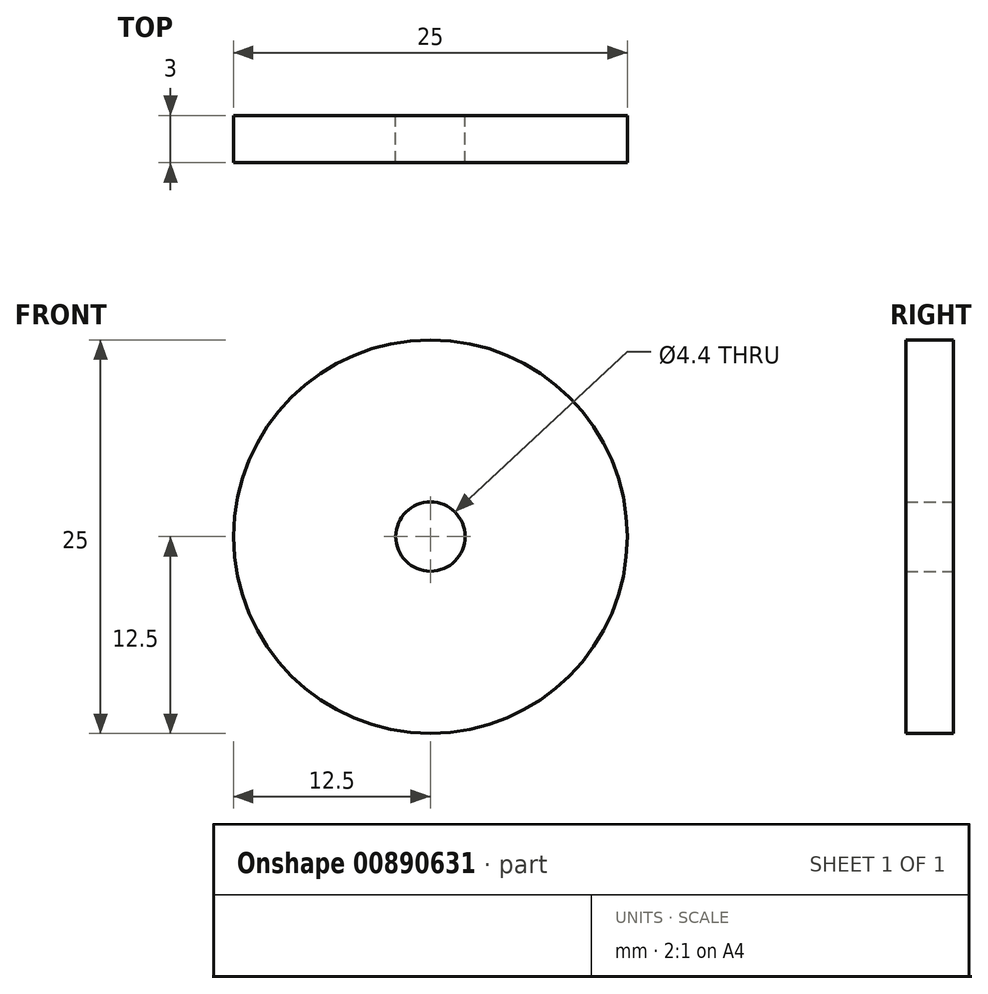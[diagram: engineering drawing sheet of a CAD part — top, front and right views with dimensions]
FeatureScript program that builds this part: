
annotation { "Feature Type Name" : "Feature", "Feature Type Description" : "" }
export const myFeature = defineFeature(function(context is Context, id is Id, definition is map)
    precondition{}
    {
        {
            var Q0;
            Q0=qCreatedBy(makeId("Front.planeOp"),FACE);
            var sketch = newSketch(context, id + "F0", { "sketchPlane" : qUnion([Q0])});
            skCircle(sketch, "E0", {"center": v(0, 0) * mm, "radius": 12.5 * mm});
            skCircle(sketch, "E1", {"center": v(0, 0) * mm, "radius": 2.2 * mm});
            skSolve(sketch);
        }
        {
            var Q0;
            Q0=makeQuery(id+"F0.imprint","IMPRINT",FACE,{"disambiguationData":[TD([[makeQuery(id+"F0.imprint","IMPRINT",EDGE,{"derivedFrom":sQuery(id+"F0.wireOp",EDGE,"E0")}),1.0]])]});
            extrude(context, id + "F1", {"entities" : qUnion([Q0]), "depth" : 3 * mm, "offsetDistance" : 25 * mm});
        }
    });
